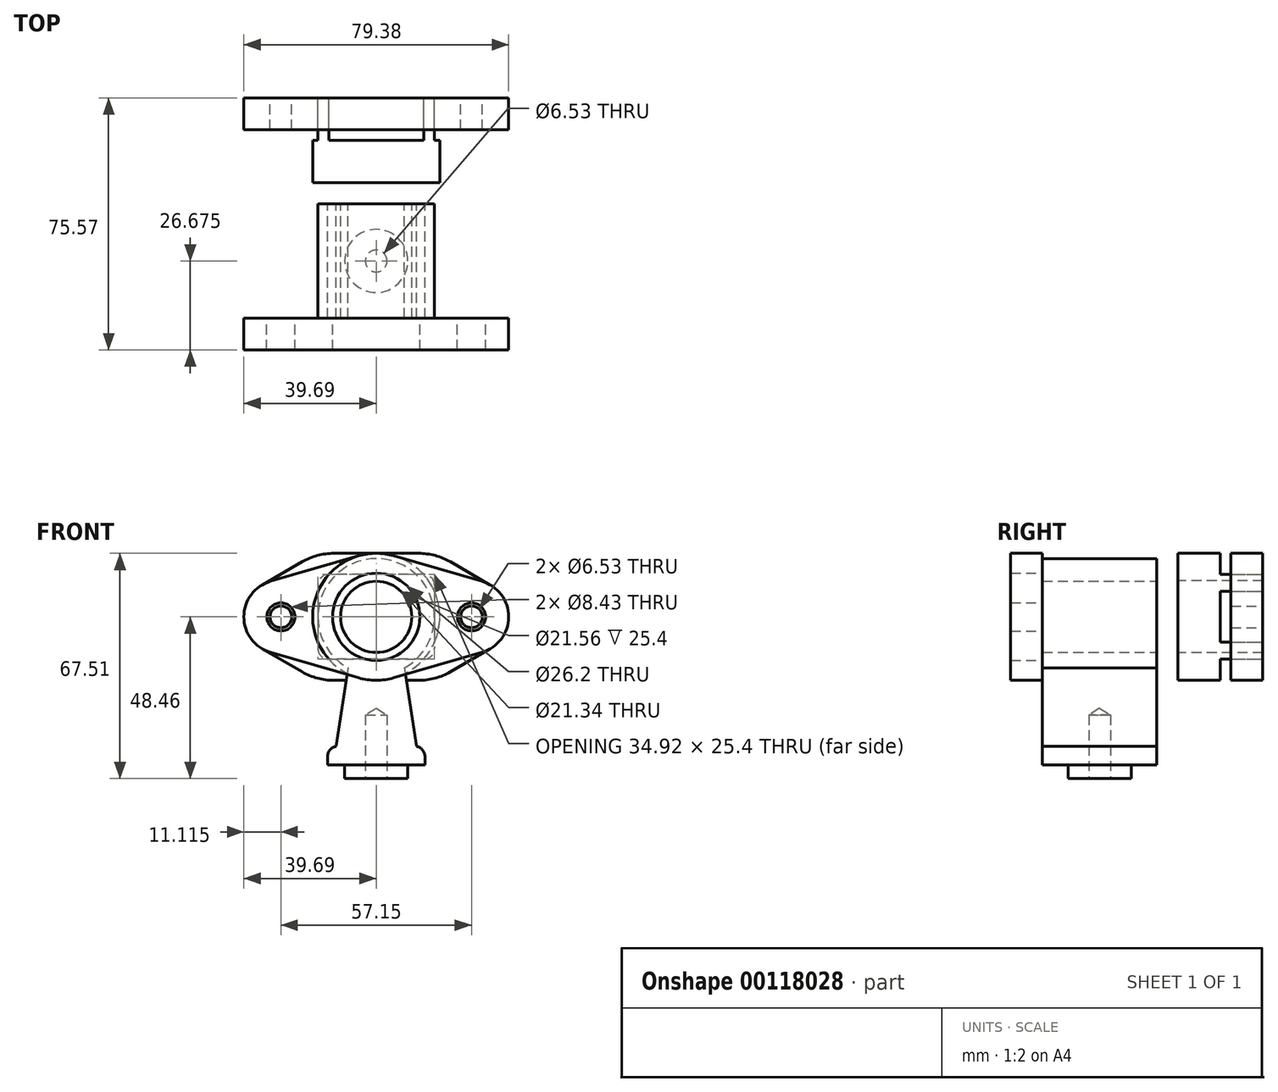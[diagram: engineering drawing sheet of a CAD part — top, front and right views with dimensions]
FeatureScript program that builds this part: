
annotation { "Feature Type Name" : "Feature", "Feature Type Description" : "" }
export const myFeature = defineFeature(function(context is Context, id is Id, definition is map)
    precondition{}
    {
        {
            var Q0;
            Q0=qCreatedBy(makeId("Front.planeOp"),FACE);
            var sketch = newSketch(context, id + "F0", { "sketchPlane" : qUnion([Q0])});
            skArc(sketch, "E0", {"start": v(8.46, -15.28) * mm, "mid": v(0, 17.46) * mm, "end": v(-8.46, -15.28) * mm});
            skLineSegment(sketch, "E1", {"start": v(-14.6, -44.4) * mm, "end": v(14.6, -44.4) * mm});
            skLineSegment(sketch, "E2", {"start": v(-14.6, -44.4) * mm, "end": v(-14.6, -41.94) * mm});
            skLineSegment(sketch, "E3", {"start": v(-14.6, -39.1) * mm, "end": v(-9.84, -39.1) * mm, "construction": true});
            skLineSegment(sketch, "E4", {"start": v(0, 0) * mm, "end": v(0, -44.4) * mm, "construction": true});
            skPoint(sketch, "E5.visualSharp", {"position": v(-14.6, -39.1) * mm});
            skArc(sketch, "E5.filletArc", {"start": v(-12.07, -38.83) * mm, "mid": v(-13.89, -39.94) * mm, "end": v(-14.6, -41.94) * mm});
            skArc(sketch, "E6.MirrorCS", {"start": v(12.07, -38.83) * mm, "mid": v(13.89, -39.94) * mm, "end": v(14.6, -41.94) * mm});
            skLineSegment(sketch, "E7.MirrorCS", {"start": v(14.6, -44.4) * mm, "end": v(14.6, -41.94) * mm});
            skCircle(sketch, "E8", {"center": v(0, 0) * mm, "radius": 10.67 * mm});
            skLineSegment(sketch, "E9", {"start": v(-8.46, -15.28) * mm, "end": v(-12.07, -38.83) * mm});
            skLineSegment(sketch, "E10", {"start": v(8.46, -15.28) * mm, "end": v(12.07, -38.83) * mm});
            skSolve(sketch);
        }
        {
            var Q0;
            Q0=makeQuery(id+"F0.imprint","IMPRINT",FACE,{"disambiguationData":[TD([[makeQuery(id+"F0.imprint","IMPRINT",EDGE,{"derivedFrom":sQuery(id+"F0.wireOp",EDGE,"E0")}),1.0]])]});
            extrude(context, id + "F1", {"entities" : qUnion([Q0]), "depth" : 34.3 * mm});
        }
        {
            var Q0;
            Q0=makeQuery(id+"F1.opExtrude","SWEPT_FACE",FACE,{"disambiguationData":[OSD([sQuery(id+"F0.wireOp",EDGE,"E1")])]});
            var sketch = newSketch(context, id + "F2", { "sketchPlane" : qUnion([Q0])});
            skCircle(sketch, "E11", {"center": v(0, 17.15) * mm, "radius": 9.46 * mm});
            skLineSegment(sketch, "E12", {"start": v(0, 17.15) * mm, "end": v(14.6, 17.15) * mm, "construction": true});
            skLineSegment(sketch, "E13", {"start": v(0, 17.15) * mm, "end": v(0, 0) * mm, "construction": true});
            skSolve(sketch);
        }
        {
            var Q0;
            Q0=makeQuery(id+"F2.imprint","IMPRINT",FACE,{"disambiguationData":[TD([[makeQuery(id+"F2.imprint","IMPRINT",EDGE,{"derivedFrom":sQuery(id+"F2.wireOp",EDGE,"E11")}),1.0]])]});
            extrude(context, id + "F3", {"entities" : qUnion([Q0]), "operationType" : NewBodyOperationType.ADD, "depth" : 4.06 * mm});
        }
        {
            var Q0;
            Q0=makeQuery(id+"F3.opExtrude","CAP_FACE",FACE,{"disambiguationData":[OSD([sQuery(id+"F2.wireOp",EDGE,"E11")])],"isStart":false});
            var sketch = newSketch(context, id + "F4", { "sketchPlane" : qUnion([Q0])});
            skPoint(sketch, "E14", {"position": v(0, 17.15) * mm});
            skSolve(sketch);
        }
        {
            var Q0;
            Q0=sQuery(id+"F4.wireOp",VERTEX,"E14");
            var Q1;
            Q1=makeQuery(id+"F1.opExtrude","SWEPT_BODY",BODY,{"disambiguationData":[OSD([sQuery(id+"F0.wireOp",EDGE,"E0"),sQuery(id+"F0.wireOp",EDGE,"E1"),sQuery(id+"F0.wireOp",EDGE,"E2"),sQuery(id+"F0.wireOp",EDGE,"E5.filletArc"),sQuery(id+"F0.wireOp",EDGE,"E6.MirrorCS"),sQuery(id+"F0.wireOp",EDGE,"E7.MirrorCS"),sQuery(id+"F0.wireOp",EDGE,"E8"),sQuery(id+"F0.wireOp",EDGE,"E9"),sQuery(id+"F0.wireOp",EDGE,"E10")])]});
            hole(context, id + "F5", {"style" : HoleStyle.SIMPLE, "endStyle" : HoleEndStyle.BLIND, "standardTappedOrClearance" : lookupTablePath({ "standard" : "ANSI", "engagement" : "75%", "pitch" : "18 tpi", "size" : "5/16", "type" : "Tapped" }), "standardBlindInLast" : lookupTablePath({ "standard" : "ANSI", "engagement" : "75%", "pitch" : "18 tpi", "size" : "5/16", "type" : "Tapped" }), "holeDiameter" : 6.53 * mm, "holeDepth" : 19.05 * mm, "locations" : qUnion([Q0]), "scope" : qUnion([Q1]), "majorDiameter" : 7.94 * mm});
        }
        {
            var Q0;
            Q0=makeQuery(id+"F1.opExtrude","CAP_FACE",FACE,{"disambiguationData":[OSD([sQuery(id+"F0.wireOp",EDGE,"E0"),sQuery(id+"F0.wireOp",EDGE,"E1"),sQuery(id+"F0.wireOp",EDGE,"E2"),sQuery(id+"F0.wireOp",EDGE,"E5.filletArc"),sQuery(id+"F0.wireOp",EDGE,"E6.MirrorCS"),sQuery(id+"F0.wireOp",EDGE,"E7.MirrorCS"),sQuery(id+"F0.wireOp",EDGE,"E8"),sQuery(id+"F0.wireOp",EDGE,"E9"),sQuery(id+"F0.wireOp",EDGE,"E10")])],"isStart":false});
            var sketch = newSketch(context, id + "F6", { "sketchPlane" : qUnion([Q0])});
            skLineSegment(sketch, "E15.bottom", {"start": v(-36.51, 19.05) * mm, "end": v(36.51, 19.05) * mm, "construction": true});
            skLineSegment(sketch, "E15.top", {"start": v(-36.51, -19.05) * mm, "end": v(36.51, -19.05) * mm, "construction": true});
            skLineSegment(sketch, "E15.left", {"start": v(-36.51, 19.05) * mm, "end": v(-36.51, -19.05) * mm, "construction": true});
            skLineSegment(sketch, "E15.right", {"start": v(36.51, 19.05) * mm, "end": v(36.51, -19.05) * mm, "construction": true});
            skLineSegment(sketch, "E16", {"start": v(0, 19.05) * mm, "end": v(0, 0) * mm, "construction": true});
            skLineSegment(sketch, "E17", {"start": v(-36.51, 0) * mm, "end": v(0, 0) * mm, "construction": true});
            skPoint(sketch, "E18", {"position": v(0, 0) * mm});
            skArc(sketch, "E19", {"start": v(31.66, -10.68) * mm, "mid": v(39.69, 0) * mm, "end": v(31.66, 10.68) * mm});
            skArc(sketch, "E20", {"start": v(5.3, 18.3) * mm, "mid": v(2.67, 18.86) * mm, "end": v(0, 19.05) * mm});
            skLineSegment(sketch, "E21", {"start": v(5.3, 18.3) * mm, "end": v(31.66, 10.68) * mm});
            skLineSegment(sketch, "E22", {"start": v(31.66, -10.68) * mm, "end": v(5.3, -18.3) * mm});
            skArc(sketch, "E23.trimOffspring", {"start": v(0, -19.05) * mm, "mid": v(2.67, -18.86) * mm, "end": v(5.3, -18.3) * mm});
            skArc(sketch, "E24.MirrorCS", {"start": v(-5.3, 18.3) * mm, "mid": v(-2.67, 18.86) * mm, "end": v(0, 19.05) * mm});
            skLineSegment(sketch, "E25.MirrorCS", {"start": v(-5.3, 18.3) * mm, "end": v(-31.66, 10.68) * mm});
            skArc(sketch, "E26.MirrorCS", {"start": v(-31.66, -10.68) * mm, "mid": v(-39.69, 0) * mm, "end": v(-31.66, 10.68) * mm});
            skLineSegment(sketch, "E27.MirrorCS", {"start": v(-31.66, -10.68) * mm, "end": v(-5.3, -18.3) * mm});
            skArc(sketch, "E28.MirrorCS", {"start": v(0, -19.05) * mm, "mid": v(-2.67, -18.86) * mm, "end": v(-5.3, -18.3) * mm});
            skSolve(sketch);
        }
        {
            var Q0;
            Q0 = qSketchRegion(id + "F6", true);
            extrude(context, id + "F7", {"entities" : qUnion([Q0]), "depth" : 9.52 * mm});
        }
        {
            var Q0;
            Q0=sQuery(id+"F6.wireOp",VERTEX,"E18");
            var Q1;
            Q1=makeQuery(id+"F7.opExtrude","SWEPT_BODY",BODY,{"disambiguationData":[OSD([sQuery(id+"F6.wireOp",EDGE,"E19"),sQuery(id+"F6.wireOp",EDGE,"E20"),sQuery(id+"F6.wireOp",EDGE,"E21"),sQuery(id+"F6.wireOp",EDGE,"E22"),sQuery(id+"F6.wireOp",EDGE,"E23.trimOffspring"),sQuery(id+"F6.wireOp",EDGE,"E24.MirrorCS"),sQuery(id+"F6.wireOp",EDGE,"E25.MirrorCS"),sQuery(id+"F6.wireOp",EDGE,"E26.MirrorCS"),sQuery(id+"F6.wireOp",EDGE,"E27.MirrorCS"),sQuery(id+"F6.wireOp",EDGE,"E28.MirrorCS")])]});
            hole(context, id + "F8", {"style" : HoleStyle.SIMPLE, "endStyle" : HoleEndStyle.THROUGH, "oppositeDirection" : true, "standardTappedOrClearance" : lookupTablePath({ "standard" : "ANSI", "fit" : "Normal (ASME)", "size" : "1", "type" : "Clearance" }), "standardBlindInLast" : lookupTablePath({ "fit" : "Free", "standard" : "ANSI", "size" : "1", "type" : "Clearance" }), "holeDiameter" : 26.2 * mm, "locations" : qUnion([Q0]), "scope" : qUnion([Q1]), "isTappedThrough" : true});
        }
        {
            var Q0;
            Q0=sQuery(id+"F6.wireOp",VERTEX,"E19.center");
            var Q1;
            Q1=sQuery(id+"F6.wireOp",VERTEX,"E26.MirrorCS.center");
            var Q2;
            Q2=makeQuery(id+"F7.opExtrude","SWEPT_BODY",BODY,{"disambiguationData":[OSD([sQuery(id+"F6.wireOp",EDGE,"E19"),sQuery(id+"F6.wireOp",EDGE,"E20"),sQuery(id+"F6.wireOp",EDGE,"E21"),sQuery(id+"F6.wireOp",EDGE,"E22"),sQuery(id+"F6.wireOp",EDGE,"E23.trimOffspring"),sQuery(id+"F6.wireOp",EDGE,"E24.MirrorCS"),sQuery(id+"F6.wireOp",EDGE,"E25.MirrorCS"),sQuery(id+"F6.wireOp",EDGE,"E26.MirrorCS"),sQuery(id+"F6.wireOp",EDGE,"E27.MirrorCS"),sQuery(id+"F6.wireOp",EDGE,"E28.MirrorCS")])]});
            hole(context, id + "F9", {"style" : HoleStyle.SIMPLE, "endStyle" : HoleEndStyle.THROUGH, "oppositeDirection" : true, "standardTappedOrClearance" : lookupTablePath({ "standard" : "ANSI", "fit" : "Normal (ASME)", "size" : "5/16", "type" : "Clearance" }), "standardBlindInLast" : lookupTablePath({ "fit" : "Free", "standard" : "ANSI", "size" : "5/16", "type" : "Clearance" }), "holeDiameter" : 8.43 * mm, "locations" : qUnion([Q0, Q1]), "scope" : qUnion([Q2]), "isTappedThrough" : true});
        }
        {
            var Q0;
            Q0=makeQuery(id+"F1.opExtrude","CAP_FACE",FACE,{"disambiguationData":[OSD([sQuery(id+"F0.wireOp",EDGE,"E0"),sQuery(id+"F0.wireOp",EDGE,"E1"),sQuery(id+"F0.wireOp",EDGE,"E2"),sQuery(id+"F0.wireOp",EDGE,"E5.filletArc"),sQuery(id+"F0.wireOp",EDGE,"E6.MirrorCS"),sQuery(id+"F0.wireOp",EDGE,"E7.MirrorCS"),sQuery(id+"F0.wireOp",EDGE,"E8"),sQuery(id+"F0.wireOp",EDGE,"E9"),sQuery(id+"F0.wireOp",EDGE,"E10")])],"isStart":true});
            cPlane(context, id + "F10", {"entities" : qUnion([Q0]), "cplaneType" : CPlaneType.OFFSET, "offset" : 6.35 * mm, "width" : 152.4 * mm, "height" : 152.4 * mm});
        }
        {
            var Q0;
            Q0=qCreatedBy(id+"F10.planeOp",FACE);
            var sketch = newSketch(context, id + "F11", { "sketchPlane" : qUnion([Q0])});
            skCircle(sketch, "E29", {"center": v(0, 0) * mm, "radius": 10.78 * mm});
            skCircle(sketch, "E30", {"center": v(0, 0) * mm, "radius": 19.05 * mm});
            skSolve(sketch);
        }
        {
            var Q0;
            Q0 = qSketchRegion(id + "F11", true);
            extrude(context, id + "F12", {"entities" : qUnion([Q0]), "depth" : 25.4 * mm});
        }
        {
            var Q0;
            Q0=makeQuery(id+"F12.opExtrude","CAP_FACE",FACE,{"disambiguationData":[OSD([sQuery(id+"F11.wireOp",EDGE,"E29"),sQuery(id+"F11.wireOp",EDGE,"E30")])],"isStart":false});
            var sketch = newSketch(context, id + "F13", { "sketchPlane" : qUnion([Q0])});
            skLineSegment(sketch, "E31.bottom", {"start": v(-17.46, 12.7) * mm, "end": v(17.46, 12.7) * mm});
            skLineSegment(sketch, "E31.top", {"start": v(-17.46, -12.7) * mm, "end": v(17.46, -12.7) * mm});
            skLineSegment(sketch, "E31.left", {"start": v(-17.46, 12.7) * mm, "end": v(-17.46, -12.7) * mm});
            skLineSegment(sketch, "E31.right", {"start": v(17.46, 12.7) * mm, "end": v(17.46, -12.7) * mm});
            skLineSegment(sketch, "E32", {"start": v(-17.46, 0) * mm, "end": v(0, 0) * mm, "construction": true});
            skLineSegment(sketch, "E33", {"start": v(0, 0) * mm, "end": v(17.46, 0) * mm, "construction": true});
            skSolve(sketch);
        }
        {
            var Q0;
            {var subQ0=sQuery(id+"F13.wireOp",EDGE,"E31.bottom");var subQ1=makeQuery(id+"F12.opExtrude","CAP_EDGE",EDGE,{"disambiguationData":[OSD([sQuery(id+"F11.wireOp",EDGE,"E30")])],"isStart":false});var subQ2=makeQuery(id+"F13.imprint","INTERSECT",VERTEX,{"disambiguationData":[OD(0.0)],"derivedFrom":[subQ1,subQ0]});Q0=makeQuery(id+"F13.imprint","IMPRINT",FACE,{"disambiguationData":[TD([[makeQuery(id+"F13.imprint","IMPRINT",EDGE,{"disambiguationData":[TD([[subQ2,-1.0]])],"derivedFrom":subQ0}),1.0]])]});}
            var Q1;
            {var subQ0=sQuery(id+"F13.wireOp",EDGE,"E31.top");var subQ1=makeQuery(id+"F12.opExtrude","CAP_EDGE",EDGE,{"disambiguationData":[OSD([sQuery(id+"F11.wireOp",EDGE,"E30")])],"isStart":false});var subQ2=makeQuery(id+"F13.imprint","INTERSECT",VERTEX,{"disambiguationData":[OD(0.0)],"derivedFrom":[subQ1,subQ0]});Q1=makeQuery(id+"F13.imprint","IMPRINT",FACE,{"disambiguationData":[TD([[makeQuery(id+"F13.imprint","IMPRINT",EDGE,{"disambiguationData":[TD([[subQ2,-1.0]])],"derivedFrom":subQ0}),-1.0]])]});}
            var Q2;
            {var subQ0=sQuery(id+"F13.wireOp",EDGE,"E31.left");var subQ1=makeQuery(id+"F12.opExtrude","CAP_EDGE",EDGE,{"disambiguationData":[OSD([sQuery(id+"F11.wireOp",EDGE,"E30")])],"isStart":false});var subQ2=makeQuery(id+"F13.imprint","INTERSECT",VERTEX,{"disambiguationData":[OD(0.0)],"derivedFrom":[subQ1,subQ0]});Q2=makeQuery(id+"F13.imprint","IMPRINT",FACE,{"disambiguationData":[TD([[makeQuery(id+"F13.imprint","IMPRINT",EDGE,{"disambiguationData":[TD([[subQ2,-1.0]])],"derivedFrom":subQ0}),-1.0]])]});}
            var Q3;
            {var subQ0=sQuery(id+"F13.wireOp",EDGE,"E31.right");var subQ1=makeQuery(id+"F12.opExtrude","CAP_EDGE",EDGE,{"disambiguationData":[OSD([sQuery(id+"F11.wireOp",EDGE,"E30")])],"isStart":false});var subQ2=makeQuery(id+"F13.imprint","INTERSECT",VERTEX,{"disambiguationData":[OD(0.0)],"derivedFrom":[subQ1,subQ0]});Q3=makeQuery(id+"F13.imprint","IMPRINT",FACE,{"disambiguationData":[TD([[makeQuery(id+"F13.imprint","IMPRINT",EDGE,{"disambiguationData":[TD([[subQ2,-1.0]])],"derivedFrom":subQ0}),1.0]])]});}
            extrude(context, id + "F14", {"entities" : qUnion([Q0, Q1, Q2, Q3]), "operationType" : NewBodyOperationType.REMOVE, "oppositeDirection" : true, "depth" : 12.7 * mm});
        }
        {
            var Q0;
            Q0=makeQuery(id+"F12.opExtrude","CAP_FACE",FACE,{"disambiguationData":[OSD([sQuery(id+"F11.wireOp",EDGE,"E29"),sQuery(id+"F11.wireOp",EDGE,"E30")])],"isStart":false});
            var sketch = newSketch(context, id + "F15", { "sketchPlane" : qUnion([Q0])});
            skLineSegment(sketch, "E34", {"start": v(-14.29, 12.7) * mm, "end": v(14.29, 12.7) * mm});
            skLineSegment(sketch, "E35", {"start": v(14.29, -12.7) * mm, "end": v(-14.29, -12.7) * mm});
            skPoint(sketch, "E36", {"position": v(0, 12.7) * mm});
            skLineSegment(sketch, "E37", {"start": v(17.46, 9.53) * mm, "end": v(17.46, -9.53) * mm});
            skLineSegment(sketch, "E38", {"start": v(-17.46, 9.53) * mm, "end": v(-17.46, -9.53) * mm});
            skPoint(sketch, "E39.visualSharp", {"position": v(-17.46, 12.7) * mm});
            skArc(sketch, "E39.filletArc", {"start": v(-14.29, 12.7) * mm, "mid": v(-16.53, 11.77) * mm, "end": v(-17.46, 9.53) * mm});
            skPoint(sketch, "E40.visualSharp", {"position": v(-17.46, -12.7) * mm});
            skArc(sketch, "E40.filletArc", {"start": v(-17.46, -9.53) * mm, "mid": v(-16.53, -11.77) * mm, "end": v(-14.29, -12.7) * mm});
            skPoint(sketch, "E41.visualSharp", {"position": v(17.46, -12.7) * mm});
            skArc(sketch, "E41.filletArc", {"start": v(14.29, -12.7) * mm, "mid": v(16.53, -11.77) * mm, "end": v(17.46, -9.53) * mm});
            skPoint(sketch, "E42.visualSharp", {"position": v(17.46, 12.7) * mm});
            skArc(sketch, "E42.filletArc", {"start": v(17.46, 9.53) * mm, "mid": v(16.53, 11.77) * mm, "end": v(14.29, 12.7) * mm});
            skLineSegment(sketch, "E43.bottom", {"start": v(-39.69, 25.4) * mm, "end": v(39.69, 25.4) * mm, "construction": true});
            skLineSegment(sketch, "E43.top", {"start": v(-39.69, -25.4) * mm, "end": v(39.69, -25.4) * mm, "construction": true});
            skLineSegment(sketch, "E43.left", {"start": v(39.69, 25.4) * mm, "end": v(39.69, -25.4) * mm, "construction": true});
            skLineSegment(sketch, "E43.right", {"start": v(-39.69, 25.4) * mm, "end": v(-39.69, -25.4) * mm, "construction": true});
            skLineSegment(sketch, "E44", {"start": v(0, 25.4) * mm, "end": v(0, 0) * mm, "construction": true});
            skLineSegment(sketch, "E45", {"start": v(0, 0) * mm, "end": v(39.69, 0) * mm, "construction": true});
            skPoint(sketch, "E46", {"position": v(0, 0) * mm});
            skArc(sketch, "E47", {"start": v(34.13, -9.62) * mm, "mid": v(39.69, 0) * mm, "end": v(34.13, 9.62) * mm});
            skLineSegment(sketch, "E48", {"start": v(22.22, 16.5) * mm, "end": v(34.13, 9.62) * mm});
            skLineSegment(sketch, "E49", {"start": v(34.13, -9.62) * mm, "end": v(22.23, -16.5) * mm});
            skLineSegment(sketch, "E50.MirrorCS", {"start": v(-22.22, 16.5) * mm, "end": v(-34.13, 9.62) * mm});
            skArc(sketch, "E51.MirrorCS", {"start": v(-34.13, -9.62) * mm, "mid": v(-39.69, 0) * mm, "end": v(-34.13, 9.62) * mm});
            skLineSegment(sketch, "E52.MirrorCS", {"start": v(-34.13, -9.62) * mm, "end": v(-22.23, -16.5) * mm});
            skLineSegment(sketch, "E53", {"start": v(-12.7, 19.05) * mm, "end": v(12.7, 19.05) * mm});
            skLineSegment(sketch, "E54", {"start": v(-12.7, -19.05) * mm, "end": v(12.7, -19.05) * mm});
            skPoint(sketch, "E55.visualSharp", {"position": v(-17.8, 19.05) * mm});
            skArc(sketch, "E55.filletArc", {"start": v(-12.7, 19.05) * mm, "mid": v(-17.63, 18.4) * mm, "end": v(-22.23, 16.5) * mm});
            skPoint(sketch, "E56.visualSharp", {"position": v(-17.8, -19.05) * mm});
            skArc(sketch, "E56.filletArc", {"start": v(-22.23, -16.5) * mm, "mid": v(-17.63, -18.4) * mm, "end": v(-12.7, -19.05) * mm});
            skPoint(sketch, "E57.visualSharp", {"position": v(17.8, -19.05) * mm});
            skArc(sketch, "E57.filletArc", {"start": v(12.7, -19.05) * mm, "mid": v(17.63, -18.4) * mm, "end": v(22.23, -16.5) * mm});
            skPoint(sketch, "E58.visualSharp", {"position": v(17.8, 19.05) * mm});
            skArc(sketch, "E58.filletArc", {"start": v(22.23, 16.5) * mm, "mid": v(17.63, 18.4) * mm, "end": v(12.7, 19.05) * mm});
            skSolve(sketch);
        }
        {
            var Q0;
            Q0 = qSketchRegion(id + "F15", true);
            extrude(context, id + "F16", {"entities" : qUnion([Q0]), "oppositeDirection" : true, "depth" : 9.52 * mm});
        }
        {
            var Q0;
            Q0=sQuery(id+"F15.wireOp",VERTEX,"E51.MirrorCS.center");
            var Q1;
            Q1=sQuery(id+"F15.wireOp",VERTEX,"E47.center");
            var Q2;
            Q2=makeQuery(id+"F16.opExtrude","SWEPT_BODY",BODY,{"disambiguationData":[OSD([sQuery(id+"F15.wireOp",EDGE,"E34"),sQuery(id+"F15.wireOp",EDGE,"E35"),sQuery(id+"F15.wireOp",EDGE,"E37"),sQuery(id+"F15.wireOp",EDGE,"E38"),sQuery(id+"F15.wireOp",EDGE,"E39.filletArc"),sQuery(id+"F15.wireOp",EDGE,"E40.filletArc"),sQuery(id+"F15.wireOp",EDGE,"E41.filletArc"),sQuery(id+"F15.wireOp",EDGE,"E42.filletArc"),sQuery(id+"F15.wireOp",EDGE,"E47"),sQuery(id+"F15.wireOp",EDGE,"e749c828-e4ee-44f3-9570-fe8026fc9bd4"),sQuery(id+"F15.wireOp",EDGE,"E48"),sQuery(id+"F15.wireOp",EDGE,"E49"),sQuery(id+"F15.wireOp",EDGE,"dbb4310e-0095-417a-8a1e-fe9d978ca0d5.trimOffspring"),sQuery(id+"F15.wireOp",EDGE,"b0a3af2e-282d-4518-a9e5-5a282897d278.MirrorCS"),sQuery(id+"F15.wireOp",EDGE,"E50.MirrorCS"),sQuery(id+"F15.wireOp",EDGE,"E51.MirrorCS"),sQuery(id+"F15.wireOp",EDGE,"E52.MirrorCS"),sQuery(id+"F15.wireOp",EDGE,"10553d37-24a8-45a9-8a98-c720d8deb526.MirrorCS")])]});
            hole(context, id + "F17", {"style" : HoleStyle.SIMPLE, "endStyle" : HoleEndStyle.THROUGH, "standardTappedOrClearance" : lookupTablePath({ "standard" : "ANSI", "engagement" : "75%", "pitch" : "18 tpi", "size" : "5/16", "type" : "Tapped" }), "standardBlindInLast" : lookupTablePath({ "standard" : "ANSI", "engagement" : "75%", "pitch" : "18 tpi", "size" : "5/16", "type" : "Tapped" }), "holeDiameter" : 6.53 * mm, "locations" : qUnion([Q0, Q1]), "scope" : qUnion([Q2]), "isTappedThrough" : true, "majorDiameter" : 7.94 * mm, "showTappedDepth" : true});
        }
    });
